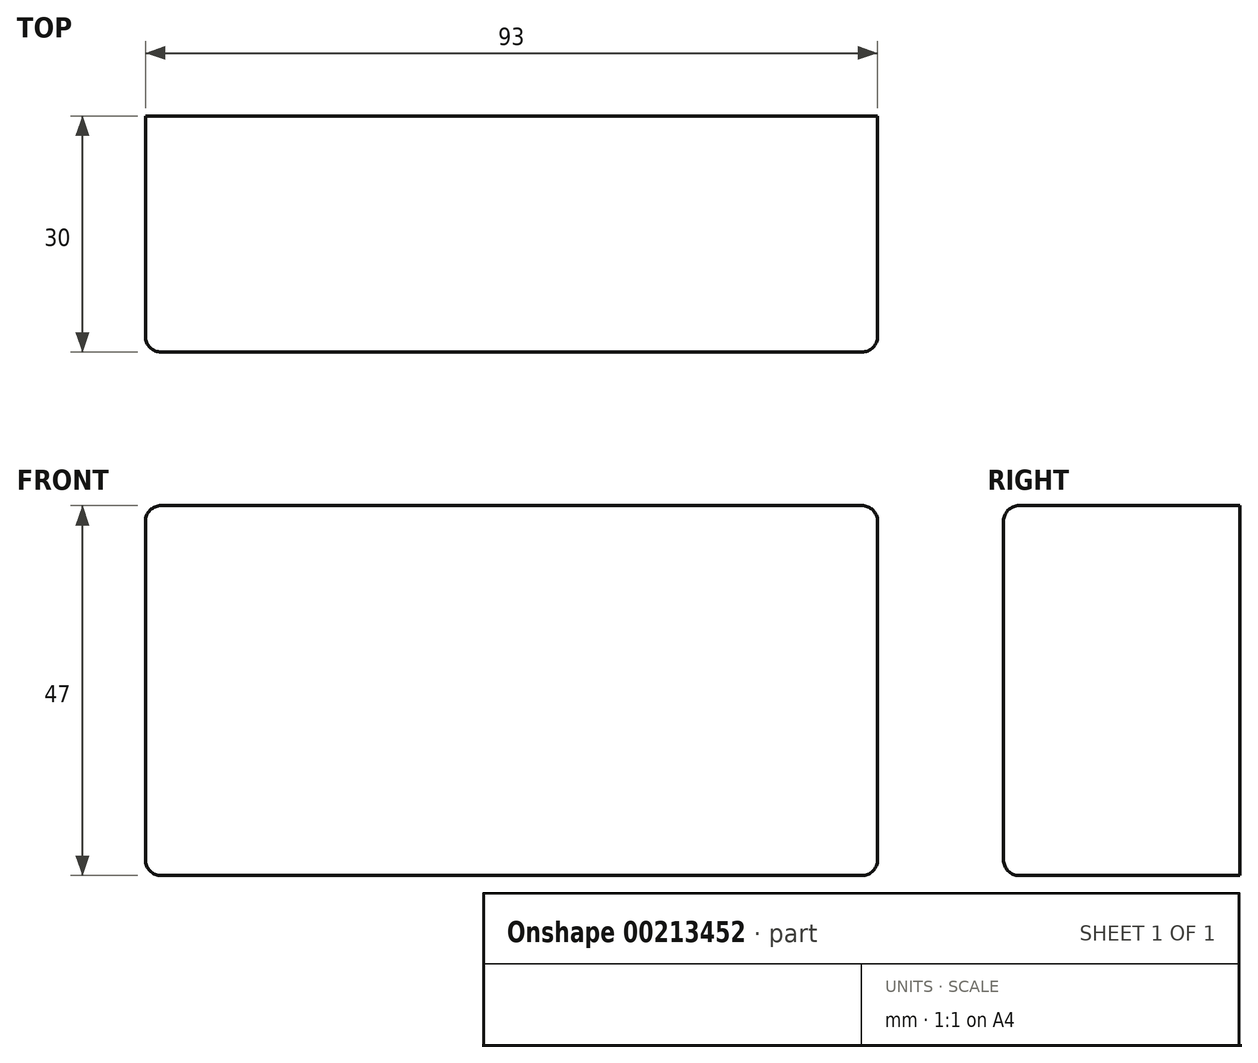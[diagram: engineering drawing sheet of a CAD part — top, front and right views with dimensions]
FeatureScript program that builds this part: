
annotation { "Feature Type Name" : "Feature", "Feature Type Description" : "" }
export const myFeature = defineFeature(function(context is Context, id is Id, definition is map)
    precondition{}
    {
        {
            var Q0;
            Q0=qCreatedBy(makeId("Front.planeOp"),FACE);
            var sketch = newSketch(context, id + "F0", { "sketchPlane" : qUnion([Q0])});
            skLineSegment(sketch, "E0.bottom", {"start": v(46.5, 23.5) * mm, "end": v(-46.5, 23.5) * mm});
            skLineSegment(sketch, "E0.top", {"start": v(46.5, -23.5) * mm, "end": v(-46.5, -23.5) * mm});
            skLineSegment(sketch, "E0.left", {"start": v(46.5, 23.5) * mm, "end": v(46.5, -23.5) * mm});
            skLineSegment(sketch, "E0.right", {"start": v(-46.5, 23.5) * mm, "end": v(-46.5, -23.5) * mm});
            skPoint(sketch, "E0.middle", {"position": v(0, 0) * mm});
            skSolve(sketch);
        }
        {
            var Q0;
            Q0=makeQuery(id+"F0.imprint","IMPRINT",FACE,{"disambiguationData":[TD([[makeQuery(id+"F0.imprint","IMPRINT",EDGE,{"derivedFrom":sQuery(id+"F0.wireOp",EDGE,"E0.bottom")}),1.0]])]});
            extrude(context, id + "F1", {"entities" : qUnion([Q0]), "depth" : 30 * mm});
        }
        {
            var Q0;
            Q0=makeQuery(id+"F1.opExtrude","CAP_FACE",FACE,{"disambiguationData":[OSD([sQuery(id+"F0.wireOp",EDGE,"E0.bottom"),sQuery(id+"F0.wireOp",EDGE,"E0.top"),sQuery(id+"F0.wireOp",EDGE,"E0.left"),sQuery(id+"F0.wireOp",EDGE,"E0.right")])],"isStart":false});
            var Q1;
            Q1=makeQuery(id+"F1.opExtrude","SWEPT_EDGE",EDGE,{"disambiguationData":[OSD([sQuery(id+"F0.wireOp",EDGE,"E0.bottom"),sQuery(id+"F0.wireOp",EDGE,"E0.right")])]});
            var Q2;
            Q2=makeQuery(id+"F1.opExtrude","SWEPT_EDGE",EDGE,{"disambiguationData":[OSD([sQuery(id+"F0.wireOp",EDGE,"E0.top"),sQuery(id+"F0.wireOp",EDGE,"E0.right")])]});
            var Q3;
            Q3=makeQuery(id+"F1.opExtrude","SWEPT_EDGE",EDGE,{"disambiguationData":[OSD([sQuery(id+"F0.wireOp",EDGE,"E0.top"),sQuery(id+"F0.wireOp",EDGE,"E0.left")])]});
            var Q4;
            Q4=makeQuery(id+"F1.opExtrude","SWEPT_EDGE",EDGE,{"disambiguationData":[OSD([sQuery(id+"F0.wireOp",EDGE,"E0.bottom"),sQuery(id+"F0.wireOp",EDGE,"E0.left")])]});
            fillet(context, id + "F2", {"entities" : qUnion([Q0, Q1, Q2, Q3, Q4]), "radius" : 2 * mm, "tangentPropagation" : true, "allowEdgeOverflow" : false});
        }
    });
